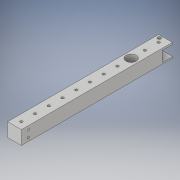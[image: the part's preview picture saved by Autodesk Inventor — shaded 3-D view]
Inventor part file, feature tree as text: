
AUTODESK INVENTOR PART (.ipt)
format: ipt  version: 2018 (Build 220112000, 112)  size: 164,352 bytes
history: native  units: in
note: dims shown in document units (in); Inventor stores cm internally (conversion verified against a paired STEP export)
features: extrude x4, sketch x4
ambient origin geometry x8: Origin, YZ Plane, XZ Plane, XY Plane, X Axis, Y Axis, Z Axis, Center Point
bodies: Solid1 (feature_tree)
feature tree (8):
  extrude  "Extrusion1"  Depth=1.0in
  extrude  "Extrusion4"  Depth=0.1875in
  extrude  "Extrusion6"  Depth=0.5in
  extrude  "Extrusion7"  Depth=0.3937in TaperAngle=0.0deg
  sketch  "Sketch1"  dims[d0=11.0in d1=1.0in]
  sketch  "Sketch4"  dims[d2=1.0in d3=0.0in d17=0.1875in]
  sketch  "Sketch6"  dims[d18=0.5in d19=0.5in]
  sketch  "Sketch7"  dims[d20=5.1181in d22=1.0in d23=0.3937in d25=1.0in d27=1.0in d28=0.0in d37=0.75in d38=0.75in d41=0.125in d42=0.125in d43=1.0in d44=0.0in d45=0.0in d46=0.25in d48=0.25in d49=2.3in d50=0.163in d51=0.163in d52=0.5in d53=0.5in d54=0.5in d56=1.0in d57=0.0in d58=0.252in]
